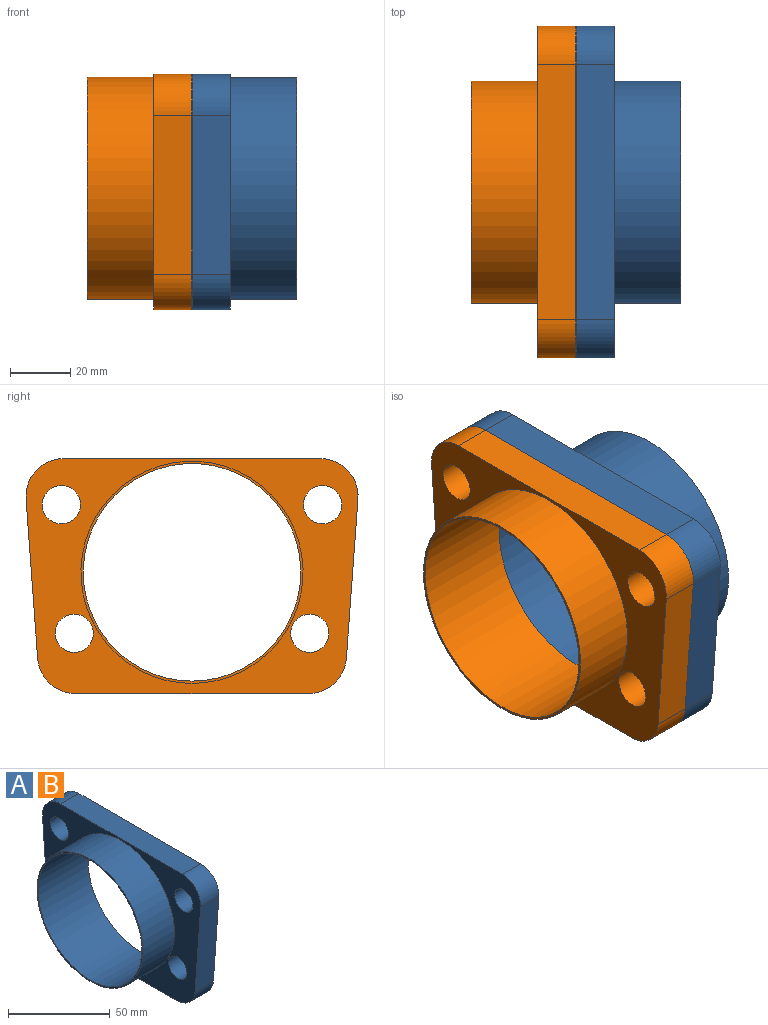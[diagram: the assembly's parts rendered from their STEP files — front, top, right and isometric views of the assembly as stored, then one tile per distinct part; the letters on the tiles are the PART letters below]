
ASSEMBLY  parts=2 mates=1
PART A: 17 faces, bbox 34.7x110.1x78 mm
  f0: plane 84.7x12.7mm, normal (0,0,1), area 1075.6mm2, adj f9,f10,f11,f12
  f1: plane 52.59x12.7mm, normal (0,-1,-0.07), area 669.6mm2, adj f9,f10,f12,f13
  f2: plane 77.03x12.7mm, normal (0,0,-1), area 978.3mm2, adj f9,f10,f13,f14
  f3: cylinder r=6.35mm len=12.7mm, axis (-1,0,0), area 506.7mm2, adj f9,f10
  f4: cylinder r=6.35mm len=12.7mm, axis (-1,0,0), area 506.7mm2, adj f9,f10
  f5: cylinder r=6.35mm len=12.7mm, axis (-1,0,0), area 506.7mm2, adj f9,f10
  f6: cylinder r=6.35mm len=12.7mm, axis (-1,0,0), area 506.7mm2, adj f9,f10
  f7: cylinder r=36.07mm len=72.14mm, axis (-1,0,0), area 7862.5mm2, adj f9,f16
  f8: plane 52.59x12.7mm, normal (0,1,-0.07), area 669.6mm2, adj f9,f10,f11,f14
  f9: plane 110.1x77.99mm, normal (1,0,0), area 3558.6mm2, adj f0,f1,f2,f3,f4,f5,f6,f7
  f10: plane 110.1x77.99mm, normal (-1,0,0), area 3384.1mm2, adj f0,f1,f2,f3,f4,f5,f6,f8
  f11: cylinder r=12.7mm len=13.62mm, axis (-1,0,0), area 265.1mm2, adj f0,f8,f9,f10
  f12: cylinder r=12.7mm len=13.62mm, axis (-1,0,0), area 265.1mm2, adj f0,f1,f9,f10
  f13: cylinder r=12.7mm len=12.7mm, axis (-1,0,0), area 241.6mm2, adj f1,f2,f9,f10
  f14: cylinder r=12.7mm len=12.7mm, axis (-1,0,0), area 241.6mm2, adj f2,f8,f9,f10
  f15: cylinder r=36.83mm len=73.66mm, axis (1,0,0), area 5089.7mm2, adj f10,f16
  f16: plane 73.66x73.66mm, normal (-1,0,0), area 174.5mm2, adj f7,f15
PART B: same geometry as A
PLACE A rot(axis=(0,0,1),180deg) t=(83.48,8.62,20.34)mm
PLACE B t=(58.08,8.62,20.34)mm
MATE fastened A.f4 <-> B.f3  axis (-1,0,0) through (70.78,-34.69,42.78)mm
